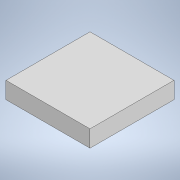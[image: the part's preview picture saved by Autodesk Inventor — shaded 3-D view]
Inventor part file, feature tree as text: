
AUTODESK INVENTOR PART (.ipt)
format: ipt  version: 2022 (Build 260153000, 153)  size: 89,088 bytes
history: native  units: mm
features: extrude x1, sketch x1
ambient origin geometry x8: Origin, YZ Plane, XZ Plane, XY Plane, X Axis, Y Axis, Z Axis, Center Point
bodies: Solid1 (feature_tree)
feature tree (2):
  extrude  "Extrusion1"  Depth=5.0mm
  sketch  "Sketch1"  dims[d0=5.0mm d1=5.0mm d2=1.0mm d3=0.0mm]
